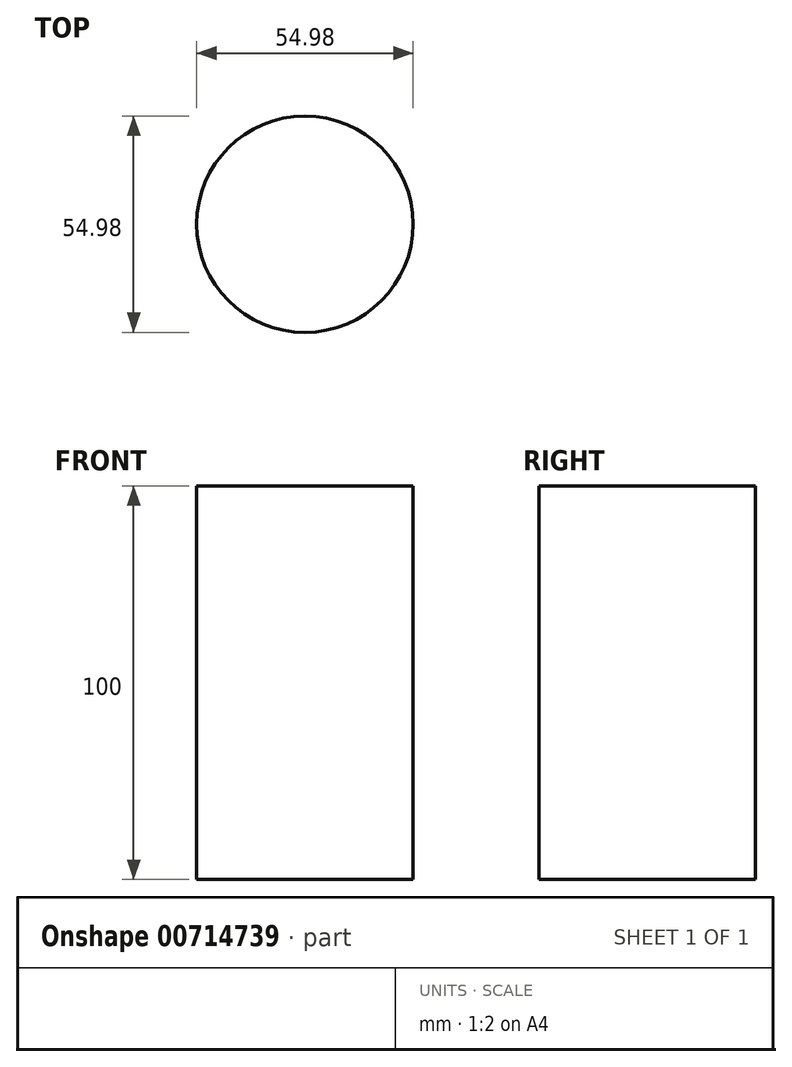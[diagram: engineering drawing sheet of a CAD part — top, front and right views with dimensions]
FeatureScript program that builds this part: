
annotation { "Feature Type Name" : "Feature", "Feature Type Description" : "" }
export const myFeature = defineFeature(function(context is Context, id is Id, definition is map)
    precondition{}
    {
        {
            var Q0;
            Q0=qCreatedBy(makeId("Top.planeOp"),FACE);
            var sketch = newSketch(context, id + "F0", { "sketchPlane" : qUnion([Q0])});
            skCircle(sketch, "E0", {"center": v(0, 0) * mm, "radius": 27.5 * mm});
            skSolve(sketch);
        }
        {
            var Q0;
            Q0 = qSketchRegion(id + "F0", true);
            extrude(context, id + "F1", {"entities" : qUnion([Q0]), "depth" : 100 * mm, "offsetDistance" : 25 * mm});
        }
    });
